# Revit family: Haworth_ComposeStorage_Cushion
name_source: partatom
category: Furniture Systems
revit_build: Autodesk Revit 2018 (Build: 20170223_1515(x64)
units: mm (PartAtom-declared; Revit-internal decimal feet)

## family parameters
Always vertical = Yes
Cut with Voids When Loaded = No
OmniClass Number = 23.40.70.14.64.21
OmniClass Title = Systems Furniture
Part Type = Normal
Room Calculation Point = No
Round Connector Dimension = Use Diameter
Shared = No
Work Plane-Based = No

## types (7) — shared parameters
Assembly Code = E2020200
Cushion Finish = Haworth _ Fabric _ Tellure _ Sky 3A-32
Custom Size = No
Description = Haworth - Compose Storage Accessories Cushion
Manufacturer = Haworth
Max. Depth = 30"
Max. Width = 36"
Min. Depth = 18"
Min. Width = 16"
Model = BZSC
Revision Number = 5
Size = Verify Final Dim. w/ Haworth
Standard Depths = 18, 24, 30 in.
Standard Widths = 16, 30, 36 in.
Sustainability Info = http://media.haworth.com
Top Thickness = 1 3/16"
URL = www.haworth.com
URL - Product = http://www.haworth.com
Warranty = http://www.haworth.com

## per-type parameters (varying)
| type | Actual Depth | Actual Width | Depth | Width |
| 36w 24d | 24" | 36" | 24" | 36" |
| 36w 18d | 18" | 36" | 18" | 36" |
| 30w 18d | 18" | 30" | 18" | 30" |
| 30w 24d | 24" | 30" | 24" | 30" |
| 16w 18d | 18" | 16" | 18" | 16" |
| 16w 24d | 24" | 16" | 24" | 16" |
| 16w 30d | 30" | 16" | 30" | 16" |

## geometry (parser evidence)
native form markers: Sweep x2
no freeform markers — native parametric forms only
